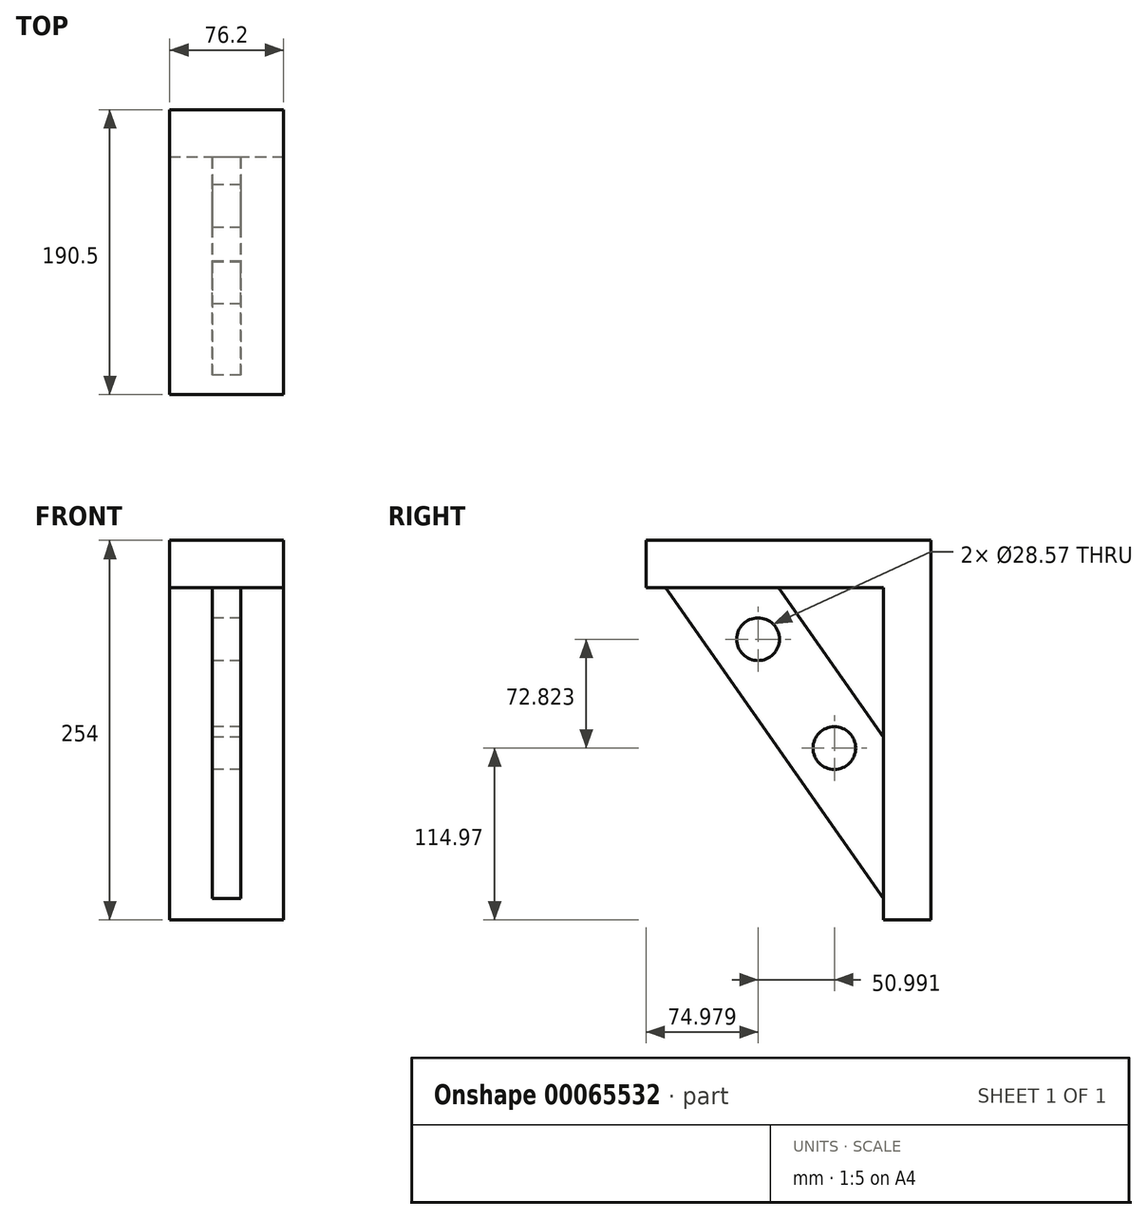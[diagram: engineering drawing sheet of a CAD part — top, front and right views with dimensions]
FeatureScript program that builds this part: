
annotation { "Feature Type Name" : "Feature", "Feature Type Description" : "" }
export const myFeature = defineFeature(function(context is Context, id is Id, definition is map)
    precondition{}
    {
        {
            var Q0;
            Q0=qCreatedBy(makeId("Right.planeOp"),FACE);
            var sketch = newSketch(context, id + "F0", { "sketchPlane" : qUnion([Q0])});
            skLineSegment(sketch, "E0.bottom", {"start": v(0, 0) * mm, "end": v(-31.75, 0) * mm});
            skLineSegment(sketch, "E0.top", {"start": v(0, -254) * mm, "end": v(-31.75, -254) * mm});
            skLineSegment(sketch, "E0.left", {"start": v(-31.75, 0) * mm, "end": v(-31.75, -254) * mm});
            skLineSegment(sketch, "E0.right", {"start": v(0, 0) * mm, "end": v(0, -254) * mm});
            skLineSegment(sketch, "E1.bottom", {"start": v(-31.75, 0) * mm, "end": v(-190.5, 0) * mm});
            skLineSegment(sketch, "E1.top", {"start": v(-31.75, -31.75) * mm, "end": v(-190.5, -31.75) * mm});
            skLineSegment(sketch, "E1.left", {"start": v(-31.75, 0) * mm, "end": v(-31.75, -31.75) * mm});
            skLineSegment(sketch, "E1.right", {"start": v(-190.5, 0) * mm, "end": v(-190.5, -31.75) * mm});
            skLineSegment(sketch, "E2", {"start": v(-177.44, -31.75) * mm, "end": v(-31.75, -239.81) * mm});
            skLineSegment(sketch, "E3", {"start": v(-31.75, -131.87) * mm, "end": v(-101.86, -31.75) * mm});
            skCircle(sketch, "E4", {"center": v(-115.52, -66.2) * mm, "radius": 14.29 * mm});
            skCircle(sketch, "E5", {"center": v(-64.53, -139.03) * mm, "radius": 14.29 * mm});
            skLineSegment(sketch, "E6", {"start": v(-31.75, -239.81) * mm, "end": v(-31.75, -131.87) * mm});
            skLineSegment(sketch, "E7", {"start": v(-101.86, -31.75) * mm, "end": v(-177.44, -31.75) * mm});
            skLineSegment(sketch, "E8", {"start": v(-139.65, -31.75) * mm, "end": v(-31.75, -185.84) * mm, "construction": true});
            skLineSegment(sketch, "E9", {"start": v(-131.9, -31.75) * mm, "end": v(-31.75, -174.77) * mm, "construction": true});
            skLineSegment(sketch, "E10", {"start": v(-31.75, -196.91) * mm, "end": v(-147.4, -31.75) * mm, "construction": true});
            skSolve(sketch);
        }
        {
            var Q0;
            Q0=makeQuery(id+"F0.imprint","IMPRINT",FACE,{"disambiguationData":[TD([[makeQuery(id+"F0.imprint","IMPRINT",EDGE,{"derivedFrom":sQuery(id+"F0.wireOp",EDGE,"E0.bottom")}),1.0]])]});
            extrude(context, id + "F1", {"entities" : qUnion([Q0]), "endBound" : BoundingType.SYMMETRIC, "depth" : 76.2 * mm});
        }
        {
            var Q0;
            Q0=makeQuery(id+"F0.imprint","IMPRINT",FACE,{"disambiguationData":[TD([[makeQuery(id+"F0.imprint","IMPRINT",EDGE,{"derivedFrom":sQuery(id+"F0.wireOp",EDGE,"E1.bottom")}),1.0]])]});
            extrude(context, id + "F2", {"entities" : qUnion([Q0]), "operationType" : NewBodyOperationType.ADD, "endBound" : BoundingType.SYMMETRIC, "depth" : 76.2 * mm});
        }
        {
            var Q0;
            Q0=makeQuery(id+"F0.imprint","IMPRINT",FACE,{"disambiguationData":[TD([[makeQuery(id+"F0.imprint","IMPRINT",EDGE,{"derivedFrom":sQuery(id+"F0.wireOp",EDGE,"E2")}),1.0]])]});
            extrude(context, id + "F3", {"entities" : qUnion([Q0]), "operationType" : NewBodyOperationType.ADD, "endBound" : BoundingType.SYMMETRIC, "depth" : 19.05 * mm});
        }
    });
